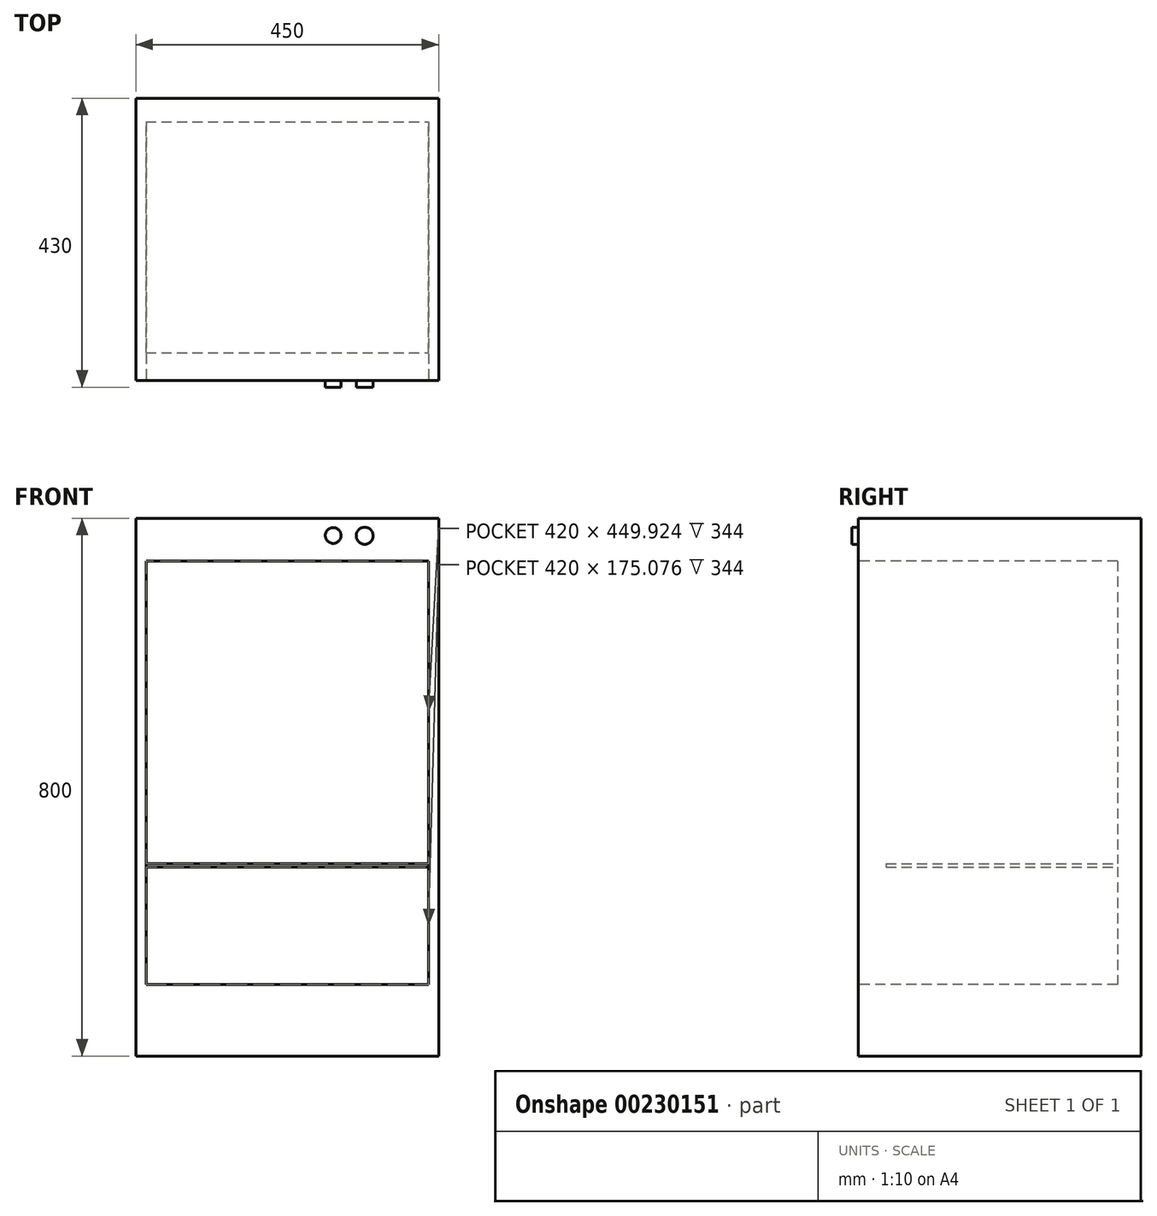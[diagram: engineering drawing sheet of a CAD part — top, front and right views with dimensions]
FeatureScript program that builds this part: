
annotation { "Feature Type Name" : "Feature", "Feature Type Description" : "" }
export const myFeature = defineFeature(function(context is Context, id is Id, definition is map)
    precondition{}
    {
        {
            var Q0;
            Q0=qCreatedBy(makeId("Top.planeOp"),FACE);
            var sketch = newSketch(context, id + "F0", { "sketchPlane" : qUnion([Q0])});
            skLineSegment(sketch, "E0.bottom", {"start": v(225, 210) * mm, "end": v(-225, 210) * mm});
            skLineSegment(sketch, "E0.top", {"start": v(225, -210) * mm, "end": v(-225, -210) * mm});
            skLineSegment(sketch, "E0.left", {"start": v(225, 210) * mm, "end": v(225, -210) * mm});
            skLineSegment(sketch, "E0.right", {"start": v(-225, 210) * mm, "end": v(-225, -210) * mm});
            skPoint(sketch, "E0.middle", {"position": v(0, 0) * mm});
            skSolve(sketch);
        }
        {
            var Q0;
            Q0 = qSketchRegion(id + "F0", true);
            extrude(context, id + "F1", {"entities" : qUnion([Q0]), "depth" : 800 * mm, "offsetDistance" : 25 * mm});
        }
        {
            var Q0;
            Q0=makeQuery(id+"F1.opExtrude","SWEPT_FACE",FACE,{"disambiguationData":[OSD([sQuery(id+"F0.wireOp",EDGE,"E0.top")])]});
            var sketch = newSketch(context, id + "F2", { "sketchPlane" : qUnion([Q0])});
            skPoint(sketch, "E1.firstSnap0", {"position": v(0, 800) * mm});
            skLineSegment(sketch, "E1.bottom", {"start": v(0, 788.21) * mm, "end": v(0, 788.21) * mm});
            skLineSegment(sketch, "E1.top", {"start": v(0, 0) * mm, "end": v(0, 0) * mm});
            skLineSegment(sketch, "E1.left", {"start": v(0, 788.21) * mm, "end": v(0, 0) * mm, "construction": true});
            skLineSegment(sketch, "E1.right", {"start": v(0, 788.21) * mm, "end": v(0, 0) * mm, "construction": true});
            skLineSegment(sketch, "E2.bottom", {"start": v(210, 736.24) * mm, "end": v(-210, 736.24) * mm});
            skLineSegment(sketch, "E2.top", {"start": v(210, 106.24) * mm, "end": v(-210, 106.24) * mm});
            skLineSegment(sketch, "E2.left", {"start": v(210, 736.24) * mm, "end": v(210, 106.24) * mm});
            skLineSegment(sketch, "E2.right", {"start": v(-210, 736.24) * mm, "end": v(-210, 106.24) * mm});
            skPoint(sketch, "E2.middle", {"position": v(0, 421.24) * mm});
            skSolve(sketch);
        }
        {
            var Q0;
            Q0 = qSketchRegion(id + "F2", true);
            extrude(context, id + "F3", {"entities" : qUnion([Q0]), "operationType" : NewBodyOperationType.REMOVE, "oppositeDirection" : true, "depth" : 385 * mm, "offsetDistance" : 25 * mm});
        }
        {
            var Q0;
            Q0=makeQuery(id+"F3.boolean.opBoolean","COPY",FACE,{"derivedFrom":makeQuery(id+"F3.opExtrude","CAP_FACE",FACE,{"disambiguationData":[OSD([sQuery(id+"F2.wireOp",EDGE,"E2.bottom"),sQuery(id+"F2.wireOp",EDGE,"E2.top"),sQuery(id+"F2.wireOp",EDGE,"E2.left"),sQuery(id+"F2.wireOp",EDGE,"E2.right")])],"isStart":false})});
            var sketch = newSketch(context, id + "F4", { "sketchPlane" : qUnion([Q0])});
            skLineSegment(sketch, "E3", {"start": v(-210, 281.32) * mm, "end": v(210, 281.32) * mm});
            skLineSegment(sketch, "E4.0", {"start": v(-210, 286.32) * mm, "end": v(210, 286.32) * mm});
            skSolve(sketch);
        }
        {
            var Q0;
            Q0 = qSketchRegion(id + "F4", true);
            var Q1;
            {var subQ0=sQuery(id+"F4.wireOp",EDGE,"E3");Q1=makeQuery(id+"F4.imprint","IMPRINT",FACE,{"disambiguationData":[TD([[makeQuery(id+"F4.imprint","IMPRINT",EDGE,{"derivedFrom":subQ0}),1.0]])]});}
            extrude(context, id + "F5", {"entities" : qUnion([Q0, Q1]), "operationType" : NewBodyOperationType.ADD, "depth" : 344 * mm, "offsetDistance" : 25 * mm});
        }
        {
            var Q0;
            Q0=makeQuery(id+"F1.opExtrude","SWEPT_FACE",FACE,{"disambiguationData":[OSD([sQuery(id+"F0.wireOp",EDGE,"E0.top")])]});
            var sketch = newSketch(context, id + "F6", { "sketchPlane" : qUnion([Q0])});
            skCircle(sketch, "E5", {"center": v(68.2, 774.36) * mm, "radius": 11.75 * mm});
            skCircle(sketch, "E6", {"center": v(115.02, 773.98) * mm, "radius": 12.66 * mm});
            skSolve(sketch);
        }
        {
            var Q0;
            Q0 = qSketchRegion(id + "F6", true);
            extrude(context, id + "F7", {"entities" : qUnion([Q0]), "operationType" : NewBodyOperationType.ADD, "depth" : 10 * mm, "offsetDistance" : 25 * mm});
        }
    });
